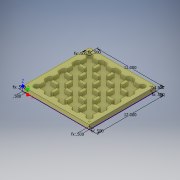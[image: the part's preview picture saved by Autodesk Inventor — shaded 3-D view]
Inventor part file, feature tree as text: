
AUTODESK INVENTOR PART (.ipt)
format: ipt  version: 2016 (Build 200138000, 138)  size: 493,568 bytes
history: native  units: in
note: dims shown in document units (in); Inventor stores cm internally (conversion verified against a paired STEP export)
features: sketch x2, extrude x2, pattern_linear x1, hole x1
ambient origin geometry x8: Origin, YZ Plane, XZ Plane, XY Plane, X Axis, Y Axis, Z Axis, Center Point
bodies: Solid1 (feature_tree)
feature tree (6):
  sketch  "Sketch1"  dims[d0=12.0in d1=12.0in]
  extrude  "Extrusion1"  Depth=12.0in
  extrude  "Extrusion3"  Depth=0.5in
  pattern_linear  "Rectangular Pattern1"  Spacing1=0.5in  [1 undecoded]
  hole  "Hole1"  [1 undecoded]
  sketch  "Sketch2"  dims[d13=0.5in d14=0.5in d15=0.5in d16=0.5in d17=0.5in d18=0.5in d19=0.5in d20=0.5in d21=0.75in d22=0.0in d25=2.04in d26=2.04in d27=1.25in d28=1.25in d29=1.0in d30=1.0in d31=1.0in d32=1.0in d33=0.7in d34=0.0in d35=1.5748in d37=2.5in d38=1.5748in d40=2.5in d41=0.25in d42=0.75in d43=0.375in d44=0.25in d45=0.5635in d46=1.0in d47=0.8108in]
note: 2 required parameter values undecoded (feature->parameter linkage not recoverable at this tier; creation-order binding heuristic only, values carry confidence <= 0.55)
